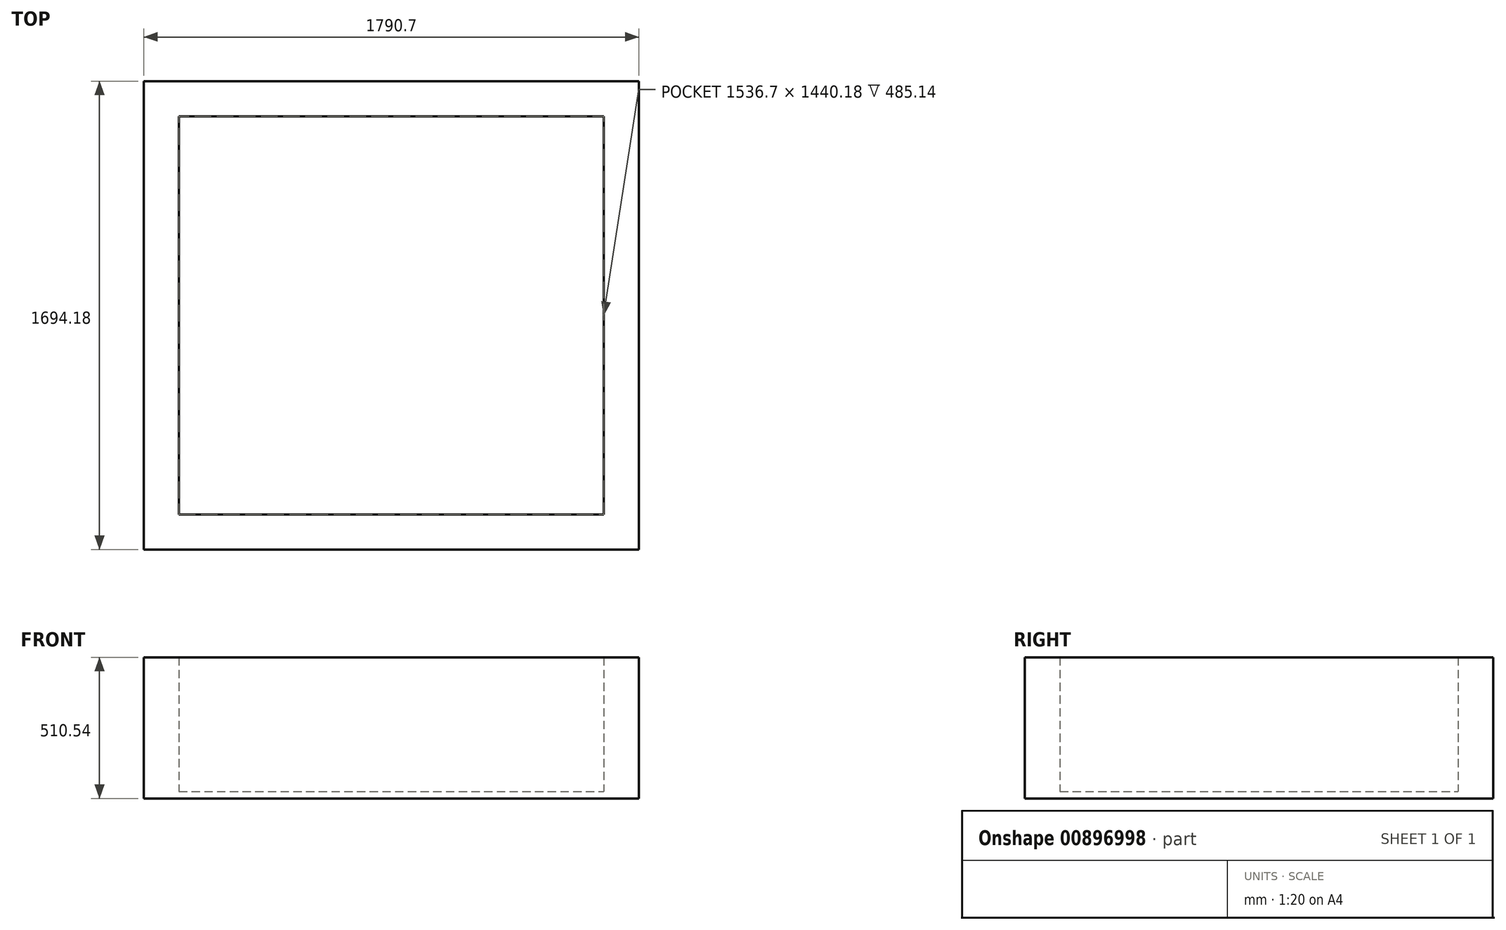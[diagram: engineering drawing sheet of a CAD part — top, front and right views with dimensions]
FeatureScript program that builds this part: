
annotation { "Feature Type Name" : "Feature", "Feature Type Description" : "" }
export const myFeature = defineFeature(function(context is Context, id is Id, definition is map)
    precondition{}
    {
        {
            var Q0;
            Q0=qCreatedBy(makeId("Top.planeOp"),FACE);
            var sketch = newSketch(context, id + "F0", { "sketchPlane" : qUnion([Q0])});
            skLineSegment(sketch, "E0.bottom", {"start": v(0, 0) * mm, "end": v(1536.7, 0) * mm});
            skLineSegment(sketch, "E0.top", {"start": v(0, 1440.18) * mm, "end": v(1536.7, 1440.18) * mm});
            skLineSegment(sketch, "E0.left", {"start": v(0, 0) * mm, "end": v(0, 1440.18) * mm});
            skLineSegment(sketch, "E0.right", {"start": v(1536.7, 0) * mm, "end": v(1536.7, 1440.18) * mm});
            skLineSegment(sketch, "E1.0", {"start": v(-127, -127) * mm, "end": v(-127, 1567.18) * mm});
            skLineSegment(sketch, "E1.1", {"start": v(-127, -127) * mm, "end": v(1663.7, -127) * mm});
            skLineSegment(sketch, "E1.2", {"start": v(1663.7, -127) * mm, "end": v(1663.7, 1567.18) * mm});
            skLineSegment(sketch, "E1.3", {"start": v(-127, 1567.18) * mm, "end": v(1663.7, 1567.18) * mm});
            skSolve(sketch);
        }
        {
            var Q0;
            Q0=makeQuery(id+"F0.imprint","IMPRINT",FACE,{"disambiguationData":[TD([[makeQuery(id+"F0.imprint","IMPRINT",EDGE,{"derivedFrom":sQuery(id+"F0.wireOp",EDGE,"E0.bottom")}),-1.0]])]});
            extrude(context, id + "F1", {"entities" : qUnion([Q0]), "depth" : 485.14 * mm, "offsetDistance" : 25.4 * mm});
        }
        {
            var Q0;
            Q0=makeQuery(id+"F0.imprint","IMPRINT",FACE,{"disambiguationData":[TD([[makeQuery(id+"F0.imprint","IMPRINT",EDGE,{"derivedFrom":sQuery(id+"F0.wireOp",EDGE,"E0.bottom")}),1.0]])]});
            var Q1;
            Q1=makeQuery(id+"F0.imprint","IMPRINT",FACE,{"disambiguationData":[TD([[makeQuery(id+"F0.imprint","IMPRINT",EDGE,{"derivedFrom":sQuery(id+"F0.wireOp",EDGE,"E0.bottom")}),-1.0]])]});
            extrude(context, id + "F2", {"entities" : qUnion([Q0, Q1]), "operationType" : NewBodyOperationType.ADD, "oppositeDirection" : true, "depth" : 25.4 * mm, "offsetDistance" : 25.4 * mm});
        }
    });
